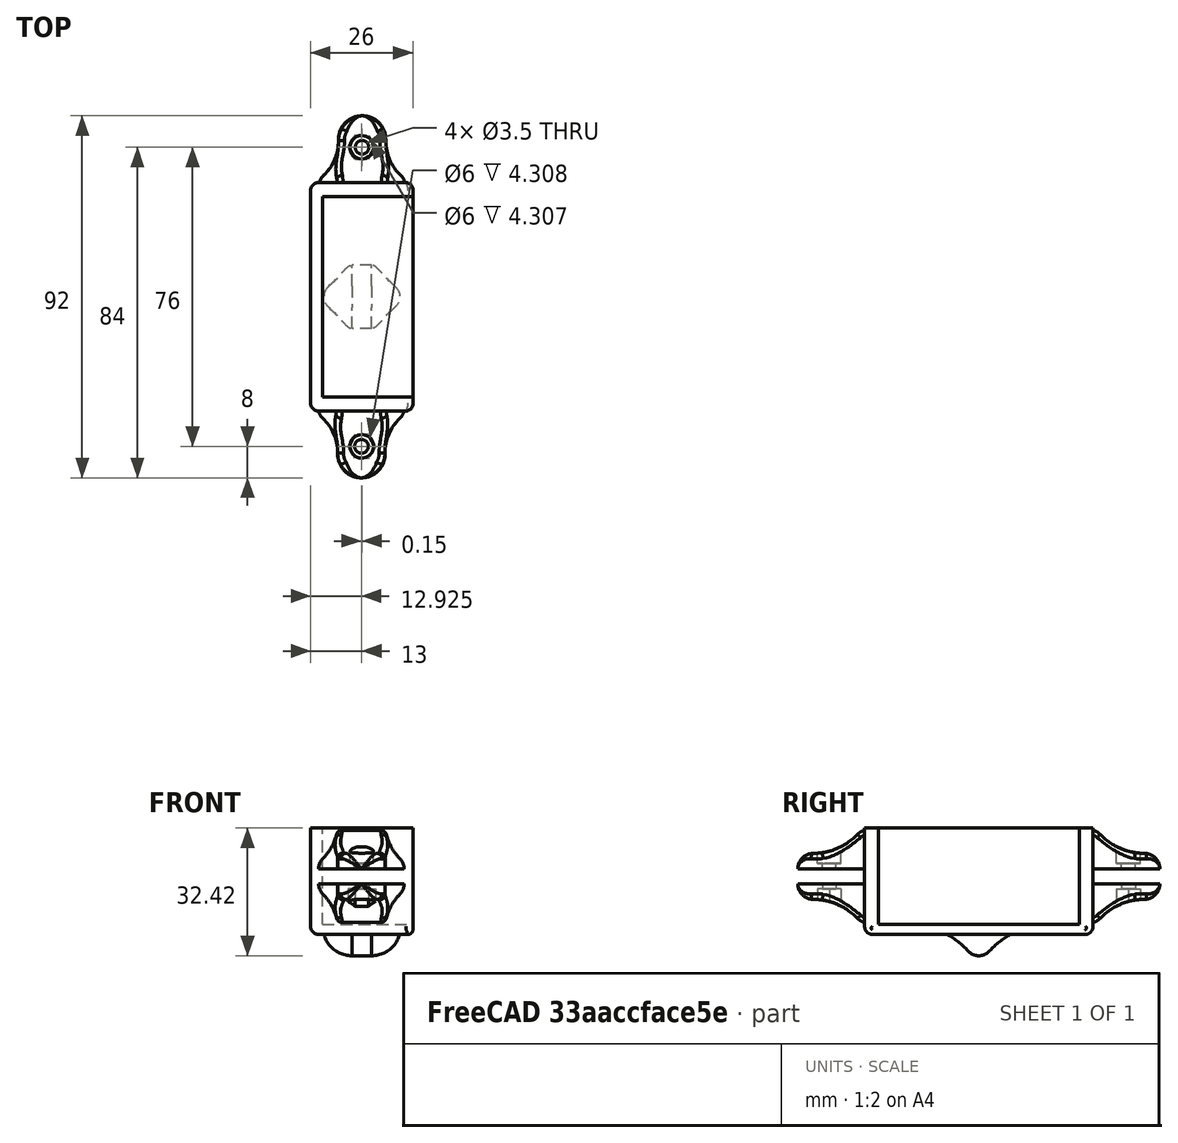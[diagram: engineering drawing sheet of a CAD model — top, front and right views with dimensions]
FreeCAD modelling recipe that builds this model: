
FCSTD DOCUMENT  (FreeCAD 0.16R6692 (Git))
Label: PortaBateriasCortado
License: All rights reserved
LicenseURL: http://es.wikipedia.org/wiki/Todos_los_derechos_reservados
objects: Sketcher::SketchObject×15, Part::MultiFuse×15, Part::Cut×12, PartDesign::Pad×9, Part::Cylinder×9, PartDesign::Revolution×6, Part::Fillet×6, Part::Box×5, Part::Sphere×2, Mesh::Feature×1, Part::Feature×1
note: 95 computed .brp shape members not serialized (recipe doc carries the construction recipe); baked Part::Feature solids carry a one-line shape summary decoded from their .brp

FEATURE [Mesh::Feature] EVOLUTION_Portapilas
FEATURE [Part::Box] Box017  label="Porta-Portapilas_Madre"
  Height = 60
  Length = 26
  Placement = pos=(-57,-29,-13) rot=(0,0,1;0rad)
  Width = 58
FEATURE [Part::Box] Box018  label="Hueco_portapilas"
  Height = 55
  Length = 26
  Placement = pos=(-54,-25.5,-10.5) rot=(0,0,1;0rad)
  Width = 51
FEATURE [Sketcher::SketchObject] Sketch014  label="Portapilas_rueda_loca"
  Placement = pos=(-46.5,0,0) rot=(0.57735,-0.57735,-0.57735;2.0944rad)
  sketch-geometry (6):
    g0: LineSegment [constr] StartX=0 StartY=0 StartZ=0 EndX=0 EndY=-13 EndZ=0
    g1: ArcOfCircle CenterX=0 CenterY=-16.7163 CenterZ=0 NormalX=0 NormalY=0 NormalZ=1 Radius=3.7 StartAngle=3.87448 EndAngle=5.55029
    g2: ArcOfCircle CenterX=17.6149 CenterY=-32.5721 CenterZ=0 NormalX=0 NormalY=0 NormalZ=1 Radius=20 StartAngle=1.77802 EndAngle=2.4087
    g3: ArcOfCircle CenterX=-17.6149 CenterY=-32.5721 CenterZ=0 NormalX=0 NormalY=0 NormalZ=1 Radius=20 StartAngle=0.73289 EndAngle=1.36357
    g4: LineSegment [constr] StartX=-2.75 StartY=-19.1917 StartZ=0 EndX=2.75 EndY=-19.1917 EndZ=0
    g5: LineSegment StartX=-13.5 StartY=-13 StartZ=0 EndX=13.5 EndY=-13 EndZ=0
  constraints (19):
    c: Coincident(g0,g-1)
    c: Vertical(g0)
    c: DistanceY(g0) = -13
    c: PointOnObject(g1,g-2)
    c: Coincident(g2,g1)
    c: Coincident(g4,g1)
    c: Horizontal(g4)
    c: Coincident(g1,g3)
    c: Symmetric(g3,g2,g0)
    c: Coincident(g4,g1)
    c: Tangent(g1,g3)
    c: Coincident(g5,g3)
    c: Coincident(g5,g2)
    c: DistanceX(g5) = 27
    c: PointOnObject(g0,g5)
    c: DistanceX(g4) = 5.5
    c: Radius(g3) = 20
    c: Equal(g2,g3)
    c: Radius(g1) = 3.7
FEATURE [PartDesign::Pad] Pad002  label="[Extrusion]_Rueda_Loca"
  Length = 5
  Length2 = 100
  Placement = pos=(-46.5,0,0) rot=(0.57735,-0.57735,-0.57735;2.0944rad)
  Reversed = true
  Sketch = -> Sketch014
  Type = 0
FEATURE [Sketcher::SketchObject] Sketch015  label="[Croquis]_Rueda_Loca_para_revolucion_1"
  Placement = pos=(-46.5,0,-13) rot=(0.57735,-0.57735,-0.57735;2.0944rad)
  sketch-geometry (5):
    g0: ArcOfCircle CenterX=0 CenterY=-3.71632 CenterZ=0 NormalX=0 NormalY=0 NormalZ=1 Radius=3.7 StartAngle=3.87448 EndAngle=5.55029
    g1: ArcOfCircle CenterX=17.6149 CenterY=-19.5721 CenterZ=0 NormalX=0 NormalY=0 NormalZ=1 Radius=20 StartAngle=1.77802 EndAngle=2.4087
    g2: ArcOfCircle CenterX=-17.6149 CenterY=-19.5721 CenterZ=0 NormalX=0 NormalY=0 NormalZ=1 Radius=20 StartAngle=0.732891 EndAngle=1.36357
    g3: LineSegment [constr] StartX=-2.75 StartY=-6.19169 StartZ=0 EndX=2.75 EndY=-6.19169 EndZ=0
    g4: LineSegment StartX=-13.5 StartY=0 StartZ=0 EndX=13.5 EndY=0 EndZ=0
  constraints (17):
    c: PointOnObject(g0,g-2)
    c: Coincident(g1,g0)
    c: Coincident(g3,g0)
    c: Horizontal(g3)
    c: Coincident(g0,g2)
    c: Coincident(g3,g0)
    c: Tangent(g0,g2)
    c: DistanceX(g3) = 5.5
    c: Radius(g2) = 20
    c: Equal(g1,g2)
    c: Radius(g0) = 3.7
    c: Coincident(g4,g2)
    c: Coincident(g4,g1)
    c: DistanceX(g4) = 27
    c: PointOnObject(g2,g-1)
    c: PointOnObject(g1,g-1)
    c: Symmetric(g2,g1,g-2)
FEATURE [PartDesign::Revolution] Revolution  label="[Revolucion]_Rueda_Loca_2"
  Angle = 90
  Axis = (0,-1,0)
  Base = (-46.5,0,-13)
  Placement = pos=(-46.5,0,-13) rot=(0.57735,-0.57735,-0.57735;2.0944rad)
  ReferenceAxis = -> Sketch015 [H_Axis]
  Reversed = true
  Sketch = -> Sketch015
FEATURE [Sketcher::SketchObject] Sketch016  label="[Croquis]_Rueda_Loca_para_revolucion_2"
  Placement = pos=(-41.5,0,-13) rot=(0.57735,-0.57735,-0.57735;2.0944rad)
  sketch-geometry (5):
    g0: ArcOfCircle CenterX=0 CenterY=-3.71632 CenterZ=0 NormalX=0 NormalY=0 NormalZ=1 Radius=3.7 StartAngle=3.87448 EndAngle=5.55029
    g1: ArcOfCircle CenterX=17.6149 CenterY=-19.5721 CenterZ=0 NormalX=0 NormalY=0 NormalZ=1 Radius=20 StartAngle=1.77802 EndAngle=2.4087
    g2: ArcOfCircle CenterX=-17.6149 CenterY=-19.5721 CenterZ=0 NormalX=0 NormalY=0 NormalZ=1 Radius=20 StartAngle=0.732891 EndAngle=1.36357
    g3: LineSegment [constr] StartX=-2.75 StartY=-6.19169 StartZ=0 EndX=2.75 EndY=-6.19169 EndZ=0
    g4: LineSegment StartX=-13.5 StartY=0 StartZ=0 EndX=13.5 EndY=-1e-12 EndZ=0
  constraints (17):
    c: PointOnObject(g0,g-2)
    c: Coincident(g1,g0)
    c: Coincident(g3,g0)
    c: Horizontal(g3)
    c: Coincident(g0,g2)
    c: Coincident(g3,g0)
    c: Tangent(g0,g2)
    c: DistanceX(g3) = 5.5
    c: Radius(g2) = 20
    c: Equal(g1,g2)
    c: Radius(g0) = 3.7
    c: Coincident(g4,g2)
    c: Coincident(g4,g1)
    c: DistanceX(g4) = 27
    c: PointOnObject(g2,g-1)
    c: PointOnObject(g1,g-1)
    c: Symmetric(g2,g1,g-2)
FEATURE [PartDesign::Revolution] Revolution001  label="[Revolucion]_Rueda_Loca_1"
  Angle = 90
  Axis = (0,-1,0)
  Base = (-41.5,0,-13)
  Placement = pos=(-41.5,0,-13) rot=(0.57735,-0.57735,-0.57735;2.0944rad)
  ReferenceAxis = -> Sketch016 [H_Axis]
  Sketch = -> Sketch016
FEATURE [Part::Sphere] Sphere  label="Porta-Portapilas_Hueco_Dedo_1"
  Angle1 = -90
  Angle2 = 90
  Angle3 = 360
  Placement = pos=(-47,35,22) rot=(0,0,1;0rad)
  Radius = 9
FEATURE [Part::Sphere] Sphere001  label="Porta-Portapilas_Hueco_Dedo_2"
  Angle1 = -90
  Angle2 = 90
  Angle3 = 360
  Placement = pos=(-47,-35,22) rot=(0,0,1;0rad)
  Radius = 9
FEATURE [Part::MultiFuse] Fusion017  label="[Union]_Porta-Portapilas_Dedo"
  Placement = pos=(0,0,2) rot=(0,0,1;0rad)
  Shapes = -> [Sphere,Sphere001]
FEATURE [Part::Cylinder] Cylinder020  label="Porta-Portapilas_Cilindro_Cables"
  Angle = 360
  Height = 4
  Placement = pos=(-43,-11.5,43) rot=(0,0,1;0rad)
  Radius = 5
FEATURE [Part::Box] Box019  label="Porta-Portapilas_Cubo_Cables"
  Height = 4
  Length = 20
  Placement = pos=(-43,-16.5,43) rot=(0,0,1;0rad)
  Width = 10
FEATURE [Sketcher::SketchObject] Sketch036
  sketch-geometry (8):
    g0: ArcOfCircle CenterX=-85.1605 CenterY=0 CenterZ=0 NormalX=0 NormalY=0 NormalZ=1 Radius=4 StartAngle=3.14159 EndAngle=3.95469
    g1: ArcOfCircle CenterX=-96.1565 CenterY=-11.6227 CenterZ=0 NormalX=0 NormalY=0 NormalZ=1 Radius=12 StartAngle=6.26222 EndAngle=7.09628
    g2: ArcOfCircle CenterX=-78.1605 CenterY=-12 CenterZ=0 NormalX=0 NormalY=0 NormalZ=1 Radius=6 StartAngle=3.12063 EndAngle=6.30415
    g3: ArcOfCircle CenterX=-71.1605 CenterY=-7.788e-09 CenterZ=0 NormalX=0 NormalY=0 NormalZ=1 Radius=4 StartAngle=5.47009 EndAngle=6.28319
    g4: ArcOfCircle CenterX=-60.1645 CenterY=-11.6227 CenterZ=0 NormalX=0 NormalY=0 NormalZ=1 Radius=12 StartAngle=2.3285 EndAngle=3.16255
    g5: LineSegment [constr] StartX=-78.1605 StartY=0 StartZ=0 EndX=-78.1605 EndY=-18 EndZ=0
    g6: LineSegment StartX=-89.1605 StartY=0 StartZ=0 EndX=-78.1605 EndY=0 EndZ=0
    g7: LineSegment StartX=-78.1605 StartY=0 StartZ=0 EndX=-67.1605 EndY=0 EndZ=0
  constraints (27):
    c: Coincident(g1,g0)
    c: Coincident(g2,g1)
    c: Coincident(g4,g3)
    c: Coincident(g4,g2)
    c: Tangent(g1,g2)
    c: Tangent(g4,g2)
    c: Tangent(g4,g3)
    c: Tangent(g1,g0)
    c: Equal(g0,g3)
    c: Vertical(g5)
    c: Symmetric(g1,g2,g5)
    c: Symmetric(g0,g3,g5)
    c: PointOnObject(g5,g2)
    c: Coincident(g6,g0)
    c: Coincident(g6,g5)
    c: Horizontal(g6)
    c: Coincident(g7,g5)
    c: Coincident(g7,g3)
    c: Horizontal(g7)
    c: DistanceX(g7) = 11
    c: Radius(g2) = 6
    c: Perpendicular(g0,g6)
    c: DistanceY(g5) = -18
    c: Radius(g1) = 12
    c: Radius(g0) = 4
    c: PointOnObject(g5,g-1)
    c: DistanceX(g-1,g3) = -67.1605
FEATURE [Sketcher::SketchObject] Sketch037
  Placement = pos=(-66,0,0) rot=(0.57735,-0.57735,-0.57735;2.0944rad)
  sketch-geometry (6):
    g0: ArcOfCircle CenterX=14.0605 CenterY=19.4746 CenterZ=0 NormalX=0 NormalY=0 NormalZ=1 Radius=15.4747 StartAngle=3.90571 EndAngle=4.70928
    g1: ArcOfCircle CenterX=0 CenterY=6 CenterZ=0 NormalX=0 NormalY=0 NormalZ=1 Radius=4 StartAngle=0.764125 EndAngle=1.5708
    g2: LineSegment StartX=0 StartY=18 StartZ=0 EndX=18 EndY=18 EndZ=0
    g3: LineSegment StartX=18 StartY=0 StartZ=0 EndX=18 EndY=18 EndZ=0
    g4: ArcOfCircle CenterX=14 CenterY=0 CenterZ=0 NormalX=0 NormalY=0 NormalZ=1 Radius=4 StartAngle=0 EndAngle=1.56769
    g5: LineSegment StartX=0 StartY=10 StartZ=0 EndX=0 EndY=18 EndZ=0
  constraints (21):
    c: Coincident(g1,g0)
    c: Tangent(g0,g1)
    c: PointOnObject(g3,g-1)
    c: PointOnObject(g1,g-2)
    c: Perpendicular(g1,g-2)
    c: Horizontal(g2)
    c: Vertical(g3)
    c: Coincident(g2,g3)
    c: PointOnObject(g4,g-1)
    c: Coincident(g4,g0)
    c: Coincident(g4,g3)
    c: Equal(g4,g1)
    c: Radius(g4) = 4
    c: Tangent(g4,g0)
    c: DistanceY(g3) = 18
    c: PointOnObject(g5,g-2)
    c: Vertical(g5)
    c: Coincident(g1,g5)
    c: Coincident(g2,g5)
    c: DistanceX(g2) = 18
    c: DistanceY(g5) = 8
FEATURE [Part::Cylinder] Cylinder045  label="Cylinder"
  Angle = 360
  Height = 10
  Placement = pos=(-44,-38,-2) rot=(0,0,1;0rad)
  Radius = 1.75
FEATURE [Part::Cylinder] Cylinder048  label="Cylinder004"
  Angle = 360
  Height = 8
  Placement = pos=(-44,-38,5) rot=(0,0,1;0rad)
  Radius = 2.75
FEATURE [Part::Feature] bq_logo007_solid  label="bq_logo002 (Solid)"
  Placement = pos=(-56,0,15) rot=(-0.57735,-0.57735,0.57735;2.0944rad)
  shape: bbox 3 x 25 x 21.48 mm, 152 faces (baked)
FEATURE [Part::MultiFuse] Fusion025  label="[Fusion]Porta-Portapilas_Cables"
  Placement = pos=(0,0,0.5) rot=(0,0,1;0rad)
  Shapes = -> [Box019,Cylinder020]
FEATURE [PartDesign::Revolution] Revolution002
  Angle = 90
  Axis = (1,0,0)
  Base = (0,0,0)
  ReferenceAxis = -> Sketch036 [H_Axis]
  Reversed = true
  Sketch = -> Sketch036
FEATURE [PartDesign::Pad] Pad017
  Length = 25
  Length2 = 100
  Placement = pos=(-66,0,0) rot=(0.57735,-0.57735,-0.57735;2.0944rad)
  Sketch = -> Sketch037
  Type = 0
FEATURE [Part::Cut] Cut048002
  Base = -> Revolution002
  Placement = pos=(34.1,-28,3.6) rot=(0,0,1;0rad)
  Tool = -> Pad017
FEATURE [Part::MultiFuse] Fusion055002
  Placement = pos=(-0.025,0,0) rot=(0,0,1;0rad)
  Shapes = -> [Cylinder048,Cylinder045]
FEATURE [Part::Fillet] Fillet036
  Base = -> Cut048002
  Edges = 2 edges r=1.5: [Edge8,Edge21]
FEATURE [Sketcher::SketchObject] Sketch049
  sketch-geometry (8):
    g0: ArcOfCircle CenterX=-85.1605 CenterY=0 CenterZ=0 NormalX=0 NormalY=0 NormalZ=1 Radius=4 StartAngle=3.14159 EndAngle=3.95469
    g1: ArcOfCircle CenterX=-96.1565 CenterY=-11.6227 CenterZ=0 NormalX=0 NormalY=0 NormalZ=1 Radius=12 StartAngle=6.26222 EndAngle=7.09628
    g2: ArcOfCircle CenterX=-78.1605 CenterY=-12 CenterZ=0 NormalX=0 NormalY=0 NormalZ=1 Radius=6 StartAngle=3.12063 EndAngle=6.30415
    g3: ArcOfCircle CenterX=-71.1605 CenterY=-7.788e-09 CenterZ=0 NormalX=0 NormalY=0 NormalZ=1 Radius=4 StartAngle=5.47009 EndAngle=6.28319
    g4: ArcOfCircle CenterX=-60.1645 CenterY=-11.6227 CenterZ=0 NormalX=0 NormalY=0 NormalZ=1 Radius=12 StartAngle=2.3285 EndAngle=3.16255
    g5: LineSegment [constr] StartX=-78.1605 StartY=0 StartZ=0 EndX=-78.1605 EndY=-18 EndZ=0
    g6: LineSegment StartX=-89.1605 StartY=0 StartZ=0 EndX=-78.1605 EndY=0 EndZ=0
    g7: LineSegment StartX=-78.1605 StartY=0 StartZ=0 EndX=-67.1605 EndY=0 EndZ=0
  constraints (27):
    c: Coincident(g1,g0)
    c: Coincident(g2,g1)
    c: Coincident(g4,g3)
    c: Coincident(g4,g2)
    c: Tangent(g1,g2)
    c: Tangent(g4,g2)
    c: Tangent(g4,g3)
    c: Tangent(g1,g0)
    c: Equal(g0,g3)
    c: Vertical(g5)
    c: Symmetric(g1,g2,g5)
    c: Symmetric(g0,g3,g5)
    c: PointOnObject(g5,g2)
    c: Coincident(g6,g0)
    c: Coincident(g6,g5)
    c: Horizontal(g6)
    c: Coincident(g7,g5)
    c: Coincident(g7,g3)
    c: Horizontal(g7)
    c: DistanceX(g7) = 11
    c: Radius(g2) = 6
    c: Perpendicular(g0,g6)
    c: DistanceY(g5) = -18
    c: Radius(g1) = 12
    c: Radius(g0) = 4
    c: PointOnObject(g5,g-1)
    c: DistanceX(g-1,g3) = -67.1605
FEATURE [Sketcher::SketchObject] Sketch050
  Placement = pos=(-66,0,0) rot=(0.57735,-0.57735,-0.57735;2.0944rad)
  sketch-geometry (6):
    g0: ArcOfCircle CenterX=14.0605 CenterY=19.4746 CenterZ=0 NormalX=0 NormalY=0 NormalZ=1 Radius=15.4747 StartAngle=3.90571 EndAngle=4.70928
    g1: ArcOfCircle CenterX=0 CenterY=6 CenterZ=0 NormalX=0 NormalY=0 NormalZ=1 Radius=4 StartAngle=0.764125 EndAngle=1.5708
    g2: LineSegment StartX=0 StartY=18 StartZ=0 EndX=18 EndY=18 EndZ=0
    g3: LineSegment StartX=18 StartY=0 StartZ=0 EndX=18 EndY=18 EndZ=0
    g4: ArcOfCircle CenterX=14 CenterY=0 CenterZ=0 NormalX=0 NormalY=0 NormalZ=1 Radius=4 StartAngle=0 EndAngle=1.56769
    g5: LineSegment StartX=0 StartY=10 StartZ=0 EndX=0 EndY=18 EndZ=0
  constraints (21):
    c: Coincident(g1,g0)
    c: Tangent(g0,g1)
    c: PointOnObject(g3,g-1)
    c: PointOnObject(g1,g-2)
    c: Perpendicular(g1,g-2)
    c: Horizontal(g2)
    c: Vertical(g3)
    c: Coincident(g2,g3)
    c: PointOnObject(g4,g-1)
    c: Coincident(g4,g0)
    c: Coincident(g4,g3)
    c: Equal(g4,g1)
    c: Radius(g4) = 4
    c: Tangent(g4,g0)
    c: DistanceY(g3) = 18
    c: PointOnObject(g5,g-2)
    c: Vertical(g5)
    c: Coincident(g1,g5)
    c: Coincident(g2,g5)
    c: DistanceX(g2) = 18
    c: DistanceY(g5) = 8
FEATURE [PartDesign::Revolution] Revolution003
  Angle = 90
  Axis = (1,0,0)
  Base = (0,0,0)
  ReferenceAxis = -> Sketch049 [H_Axis]
  Reversed = true
  Sketch = -> Sketch049
FEATURE [PartDesign::Pad] Pad018
  Length = 25
  Length2 = 100
  Placement = pos=(-66,0,0) rot=(0.57735,-0.57735,-0.57735;2.0944rad)
  Sketch = -> Sketch050
  Type = 0
FEATURE [Part::Cut] Cut048003
  Base = -> Revolution003
  Placement = pos=(34.1,-28,3.6) rot=(0,0,1;0rad)
  Tool = -> Pad018
FEATURE [Part::Fillet] Fillet037
  Base = -> Cut048003
  Edges = 2 edges r=1.5: [Edge8,Edge21]
FEATURE [Part::Cut] Cut048004  label="Rail_superior"
  Base = -> Fillet036
  Placement = pos=(-0.05,0,0) rot=(0,0,1;0rad)
  Tool = -> Fusion055002
FEATURE [Part::Cylinder] Cylinder054  label="Cylinder058"
  Angle = 360
  Height = 10
  Placement = pos=(-44,-38,-2) rot=(0,0,1;0rad)
  Radius = 1.75
FEATURE [Sketcher::SketchObject] Sketch051
  Placement = pos=(-44,-38,13) rot=(0,0,1;0rad)
  sketch-geometry (7):
    g0: LineSegment StartX=-1.65 StartY=2.85788 StartZ=0 EndX=-3.3 EndY=0 EndZ=0
    g1: LineSegment StartX=-3.3 StartY=0 StartZ=0 EndX=-1.65 EndY=-2.85788 EndZ=0
    g2: LineSegment StartX=-1.65 StartY=-2.85788 StartZ=0 EndX=1.65 EndY=-2.85788 EndZ=0
    g3: LineSegment StartX=1.65 StartY=-2.85788 StartZ=0 EndX=3.3 EndY=0 EndZ=0
    g4: LineSegment StartX=3.3 StartY=0 StartZ=0 EndX=1.65 EndY=2.85788 EndZ=0
    g5: LineSegment StartX=1.65 StartY=2.85788 StartZ=0 EndX=-1.65 EndY=2.85788 EndZ=0
    g6: Circle [constr] CenterX=0 CenterY=0 CenterZ=0 NormalX=0 NormalY=0 NormalZ=1 Radius=3.3
  constraints (17):
    c: Coincident(g0,g1)
    c: Coincident(g1,g2)
    c: Coincident(g2,g3)
    c: Coincident(g3,g4)
    c: Coincident(g4,g5)
    c: Coincident(g5,g0)
    c: Equal(g0, g1-g5) x5
    c: PointOnObject(g0,g6)
    c: PointOnObject(g1,g6)
    c: PointOnObject(g2,g6)
    c: PointOnObject(g3,g6)
    c: PointOnObject(g4,g6)
    c: PointOnObject(g5,g6)
    c: Coincident(g3,g-1)
    c: Radius(g6) = 3.3
    c: Horizontal(g5)
    c: Coincident(g6,g-1)
FEATURE [PartDesign::Pad] Pad019
  Length = 8
  Length2 = 100
  Placement = pos=(-44,-38,13) rot=(0,0,1;0rad)
  Reversed = true
  Sketch = -> Sketch051
  Type = 0
FEATURE [Part::MultiFuse] Fusion055003
  Placement = pos=(-0.075,0,0) rot=(0,0,1;0rad)
  Shapes = -> [Pad019,Cylinder054]
FEATURE [Part::Cut] Cut048005  label="Rail_inferior"
  Base = -> Fillet037
  Placement = pos=(-88.15,0,3.5) rot=(0,1,0;3.14159rad)
  Tool = -> Fusion055003
FEATURE [Part::MultiFuse] Fusion055004  label="Rail_izquierdo"
  Shapes = -> [Cut048004,Cut048005]
FEATURE [Sketcher::SketchObject] Sketch052
  sketch-geometry (8):
    g0: ArcOfCircle CenterX=-85.1605 CenterY=0 CenterZ=0 NormalX=0 NormalY=0 NormalZ=1 Radius=4 StartAngle=3.14159 EndAngle=3.95469
    g1: ArcOfCircle CenterX=-96.1565 CenterY=-11.6227 CenterZ=0 NormalX=0 NormalY=0 NormalZ=1 Radius=12 StartAngle=6.26222 EndAngle=7.09628
    g2: ArcOfCircle CenterX=-78.1605 CenterY=-12 CenterZ=0 NormalX=0 NormalY=0 NormalZ=1 Radius=6 StartAngle=3.12063 EndAngle=6.30415
    g3: ArcOfCircle CenterX=-71.1605 CenterY=-7.788e-09 CenterZ=0 NormalX=0 NormalY=0 NormalZ=1 Radius=4 StartAngle=5.47009 EndAngle=6.28319
    g4: ArcOfCircle CenterX=-60.1645 CenterY=-11.6227 CenterZ=0 NormalX=0 NormalY=0 NormalZ=1 Radius=12 StartAngle=2.3285 EndAngle=3.16255
    g5: LineSegment [constr] StartX=-78.1605 StartY=0 StartZ=0 EndX=-78.1605 EndY=-18 EndZ=0
    g6: LineSegment StartX=-89.1605 StartY=0 StartZ=0 EndX=-78.1605 EndY=0 EndZ=0
    g7: LineSegment StartX=-78.1605 StartY=0 StartZ=0 EndX=-67.1605 EndY=0 EndZ=0
  constraints (27):
    c: Coincident(g1,g0)
    c: Coincident(g2,g1)
    c: Coincident(g4,g3)
    c: Coincident(g4,g2)
    c: Tangent(g1,g2)
    c: Tangent(g4,g2)
    c: Tangent(g4,g3)
    c: Tangent(g1,g0)
    c: Equal(g0,g3)
    c: Vertical(g5)
    c: Symmetric(g1,g2,g5)
    c: Symmetric(g0,g3,g5)
    c: PointOnObject(g5,g2)
    c: Coincident(g6,g0)
    c: Coincident(g6,g5)
    c: Horizontal(g6)
    c: Coincident(g7,g5)
    c: Coincident(g7,g3)
    c: Horizontal(g7)
    c: DistanceX(g7) = 11
    c: Radius(g2) = 6
    c: Perpendicular(g0,g6)
    c: DistanceY(g5) = -18
    c: Radius(g1) = 12
    c: Radius(g0) = 4
    c: PointOnObject(g5,g-1)
    c: DistanceX(g-1,g3) = -67.1605
FEATURE [Sketcher::SketchObject] Sketch053
  Placement = pos=(-66,0,0) rot=(0.57735,-0.57735,-0.57735;2.0944rad)
  sketch-geometry (6):
    g0: ArcOfCircle CenterX=14.0605 CenterY=19.4746 CenterZ=0 NormalX=0 NormalY=0 NormalZ=1 Radius=15.4747 StartAngle=3.90571 EndAngle=4.70928
    g1: ArcOfCircle CenterX=0 CenterY=6 CenterZ=0 NormalX=0 NormalY=0 NormalZ=1 Radius=4 StartAngle=0.764125 EndAngle=1.5708
    g2: LineSegment StartX=0 StartY=18 StartZ=0 EndX=18 EndY=18 EndZ=0
    g3: LineSegment StartX=18 StartY=0 StartZ=0 EndX=18 EndY=18 EndZ=0
    g4: ArcOfCircle CenterX=14 CenterY=0 CenterZ=0 NormalX=0 NormalY=0 NormalZ=1 Radius=4 StartAngle=0 EndAngle=1.56769
    g5: LineSegment StartX=0 StartY=10 StartZ=0 EndX=0 EndY=18 EndZ=0
  constraints (21):
    c: Coincident(g1,g0)
    c: Tangent(g0,g1)
    c: PointOnObject(g3,g-1)
    c: PointOnObject(g1,g-2)
    c: Perpendicular(g1,g-2)
    c: Horizontal(g2)
    c: Vertical(g3)
    c: Coincident(g2,g3)
    c: PointOnObject(g4,g-1)
    c: Coincident(g4,g0)
    c: Coincident(g4,g3)
    c: Equal(g4,g1)
    c: Radius(g4) = 4
    c: Tangent(g4,g0)
    c: DistanceY(g3) = 18
    c: PointOnObject(g5,g-2)
    c: Vertical(g5)
    c: Coincident(g1,g5)
    c: Coincident(g2,g5)
    c: DistanceX(g2) = 18
    c: DistanceY(g5) = 8
FEATURE [Part::Cylinder] Cylinder055  label="Cylinder062"
  Angle = 360
  Height = 10
  Placement = pos=(-44,-38,-2) rot=(0,0,1;0rad)
  Radius = 1.75
FEATURE [Part::Cylinder] Cylinder056  label="Cylinder060"
  Angle = 360
  Height = 8
  Placement = pos=(-44,-38,5) rot=(0,0,1;0rad)
  Radius = 2.75
FEATURE [PartDesign::Revolution] Revolution004
  Angle = 90
  Axis = (1,0,0)
  Base = (0,0,0)
  ReferenceAxis = -> Sketch052 [H_Axis]
  Reversed = true
  Sketch = -> Sketch052
FEATURE [PartDesign::Pad] Pad020
  Length = 25
  Length2 = 100
  Placement = pos=(-66,0,0) rot=(0.57735,-0.57735,-0.57735;2.0944rad)
  Sketch = -> Sketch053
  Type = 0
FEATURE [Part::Cut] Cut048006
  Base = -> Revolution004
  Placement = pos=(34.1,-28,3.6) rot=(0,0,1;0rad)
  Tool = -> Pad020
FEATURE [Part::MultiFuse] Fusion055005
  Placement = pos=(-0.025,0,0) rot=(0,0,1;0rad)
  Shapes = -> [Cylinder056,Cylinder055]
FEATURE [Part::Fillet] Fillet038
  Base = -> Cut048006
  Edges = 2 edges r=1.5: [Edge8,Edge21]
FEATURE [Sketcher::SketchObject] Sketch054
  sketch-geometry (8):
    g0: ArcOfCircle CenterX=-85.1605 CenterY=0 CenterZ=0 NormalX=0 NormalY=0 NormalZ=1 Radius=4 StartAngle=3.14159 EndAngle=3.95469
    g1: ArcOfCircle CenterX=-96.1565 CenterY=-11.6227 CenterZ=0 NormalX=0 NormalY=0 NormalZ=1 Radius=12 StartAngle=6.26222 EndAngle=7.09628
    g2: ArcOfCircle CenterX=-78.1605 CenterY=-12 CenterZ=0 NormalX=0 NormalY=0 NormalZ=1 Radius=6 StartAngle=3.12063 EndAngle=6.30415
    g3: ArcOfCircle CenterX=-71.1605 CenterY=-7.788e-09 CenterZ=0 NormalX=0 NormalY=0 NormalZ=1 Radius=4 StartAngle=5.47009 EndAngle=6.28319
    g4: ArcOfCircle CenterX=-60.1645 CenterY=-11.6227 CenterZ=0 NormalX=0 NormalY=0 NormalZ=1 Radius=12 StartAngle=2.3285 EndAngle=3.16255
    g5: LineSegment [constr] StartX=-78.1605 StartY=0 StartZ=0 EndX=-78.1605 EndY=-18 EndZ=0
    g6: LineSegment StartX=-89.1605 StartY=0 StartZ=0 EndX=-78.1605 EndY=0 EndZ=0
    g7: LineSegment StartX=-78.1605 StartY=0 StartZ=0 EndX=-67.1605 EndY=0 EndZ=0
  constraints (27):
    c: Coincident(g1,g0)
    c: Coincident(g2,g1)
    c: Coincident(g4,g3)
    c: Coincident(g4,g2)
    c: Tangent(g1,g2)
    c: Tangent(g4,g2)
    c: Tangent(g4,g3)
    c: Tangent(g1,g0)
    c: Equal(g0,g3)
    c: Vertical(g5)
    c: Symmetric(g1,g2,g5)
    c: Symmetric(g0,g3,g5)
    c: PointOnObject(g5,g2)
    c: Coincident(g6,g0)
    c: Coincident(g6,g5)
    c: Horizontal(g6)
    c: Coincident(g7,g5)
    c: Coincident(g7,g3)
    c: Horizontal(g7)
    c: DistanceX(g7) = 11
    c: Radius(g2) = 6
    c: Perpendicular(g0,g6)
    c: DistanceY(g5) = -18
    c: Radius(g1) = 12
    c: Radius(g0) = 4
    c: PointOnObject(g5,g-1)
    c: DistanceX(g-1,g3) = -67.1605
FEATURE [Sketcher::SketchObject] Sketch055
  Placement = pos=(-66,0,0) rot=(0.57735,-0.57735,-0.57735;2.0944rad)
  sketch-geometry (6):
    g0: ArcOfCircle CenterX=14.0605 CenterY=19.4746 CenterZ=0 NormalX=0 NormalY=0 NormalZ=1 Radius=15.4747 StartAngle=3.90571 EndAngle=4.70928
    g1: ArcOfCircle CenterX=0 CenterY=6 CenterZ=0 NormalX=0 NormalY=0 NormalZ=1 Radius=4 StartAngle=0.764125 EndAngle=1.5708
    g2: LineSegment StartX=0 StartY=18 StartZ=0 EndX=18 EndY=18 EndZ=0
    g3: LineSegment StartX=18 StartY=0 StartZ=0 EndX=18 EndY=18 EndZ=0
    g4: ArcOfCircle CenterX=14 CenterY=0 CenterZ=0 NormalX=0 NormalY=0 NormalZ=1 Radius=4 StartAngle=0 EndAngle=1.56769
    g5: LineSegment StartX=0 StartY=10 StartZ=0 EndX=0 EndY=18 EndZ=0
  constraints (21):
    c: Coincident(g1,g0)
    c: Tangent(g0,g1)
    c: PointOnObject(g3,g-1)
    c: PointOnObject(g1,g-2)
    c: Perpendicular(g1,g-2)
    c: Horizontal(g2)
    c: Vertical(g3)
    c: Coincident(g2,g3)
    c: PointOnObject(g4,g-1)
    c: Coincident(g4,g0)
    c: Coincident(g4,g3)
    c: Equal(g4,g1)
    c: Radius(g4) = 4
    c: Tangent(g4,g0)
    c: DistanceY(g3) = 18
    c: PointOnObject(g5,g-2)
    c: Vertical(g5)
    c: Coincident(g1,g5)
    c: Coincident(g2,g5)
    c: DistanceX(g2) = 18
    c: DistanceY(g5) = 8
FEATURE [PartDesign::Revolution] Revolution005
  Angle = 90
  Axis = (1,0,0)
  Base = (0,0,0)
  ReferenceAxis = -> Sketch054 [H_Axis]
  Reversed = true
  Sketch = -> Sketch054
FEATURE [PartDesign::Pad] Pad021
  Length = 25
  Length2 = 100
  Placement = pos=(-66,0,0) rot=(0.57735,-0.57735,-0.57735;2.0944rad)
  Sketch = -> Sketch055
  Type = 0
FEATURE [Part::Cut] Cut048007
  Base = -> Revolution005
  Placement = pos=(34.1,-28,3.6) rot=(0,0,1;0rad)
  Tool = -> Pad021
FEATURE [Part::Fillet] Fillet039
  Base = -> Cut048007
  Edges = 2 edges r=1.5: [Edge8,Edge21]
FEATURE [Part::Cut] Cut048008  label="Rail_superior001"
  Base = -> Fillet038
  Placement = pos=(-0.05,0,0) rot=(0,0,1;0rad)
  Tool = -> Fusion055005
FEATURE [Part::Cylinder] Cylinder057  label="Cylinder063"
  Angle = 360
  Height = 10
  Placement = pos=(-44,-38,-2) rot=(0,0,1;0rad)
  Radius = 1.75
FEATURE [Sketcher::SketchObject] Sketch056
  Placement = pos=(-44,-38,13) rot=(0,0,1;0rad)
  sketch-geometry (7):
    g0: LineSegment StartX=-1.65 StartY=2.85788 StartZ=0 EndX=-3.3 EndY=0 EndZ=0
    g1: LineSegment StartX=-3.3 StartY=0 StartZ=0 EndX=-1.65 EndY=-2.85788 EndZ=0
    g2: LineSegment StartX=-1.65 StartY=-2.85788 StartZ=0 EndX=1.65 EndY=-2.85788 EndZ=0
    g3: LineSegment StartX=1.65 StartY=-2.85788 StartZ=0 EndX=3.3 EndY=0 EndZ=0
    g4: LineSegment StartX=3.3 StartY=0 StartZ=0 EndX=1.65 EndY=2.85788 EndZ=0
    g5: LineSegment StartX=1.65 StartY=2.85788 StartZ=0 EndX=-1.65 EndY=2.85788 EndZ=0
    g6: Circle [constr] CenterX=0 CenterY=0 CenterZ=0 NormalX=0 NormalY=0 NormalZ=1 Radius=3.3
  constraints (17):
    c: Coincident(g0,g1)
    c: Coincident(g1,g2)
    c: Coincident(g2,g3)
    c: Coincident(g3,g4)
    c: Coincident(g4,g5)
    c: Coincident(g5,g0)
    c: Equal(g0, g1-g5) x5
    c: PointOnObject(g0,g6)
    c: PointOnObject(g1,g6)
    c: PointOnObject(g2,g6)
    c: PointOnObject(g3,g6)
    c: PointOnObject(g4,g6)
    c: PointOnObject(g5,g6)
    c: Coincident(g3,g-1)
    c: Radius(g6) = 3.3
    c: Horizontal(g5)
    c: Coincident(g6,g-1)
FEATURE [PartDesign::Pad] Pad022
  Length = 8
  Length2 = 100
  Placement = pos=(-44,-38,13) rot=(0,0,1;0rad)
  Reversed = true
  Sketch = -> Sketch056
  Type = 0
FEATURE [Part::MultiFuse] Fusion055006
  Placement = pos=(-0.075,0,0) rot=(0,0,1;0rad)
  Shapes = -> [Pad022,Cylinder057]
FEATURE [Part::Cut] Cut048009  label="Rail_inferior001"
  Base = -> Fillet039
  Placement = pos=(-88.15,0,3.5) rot=(0,1,0;3.14159rad)
  Tool = -> Fusion055006
FEATURE [Part::MultiFuse] Fusion055007  label="Rail_iderecho"
  Placement = pos=(-88,0,0) rot=(0,0,1;3.14159rad)
  Shapes = -> [Cut048008,Cut048009]
FEATURE [Part::MultiFuse] Fusion055008  label="Rueda_loca"
  Placement = pos=(0,0,2) rot=(0,0,1;0rad)
  Shapes = -> [Pad002,Revolution001,Revolution]
FEATURE [Part::MultiFuse] Fusion055009  label="Huecos_portapilas"
  Shapes = -> [Box018,bq_logo007_solid,Fusion025]
FEATURE [Part::Cut] Cut048010
  Base = -> Box017
  Tool = -> Fusion055009
FEATURE [Part::Fillet] Fillet040
  Base = -> Cut048010
  Edges = 17 edges: [Edge1 r=2,Edge2 r=2,Edge3 r=2,Edge4 r=2,Edge103 r=2,Edge104 r=1.8,Edge105 r=2,Edge106 r=2,Edge107 r=1.2,Edge108 r=1.2,Edge109 r=1.2,Edge110 r=1.2,Edge111 r=1.2,Edge112 r=2,Edge113 r=1.2,Edge114 r=1.8,Edge322 r=1.2]
FEATURE [Part::Cut] Cut048011
  Base = -> Fillet040
  Tool = -> Fusion017
FEATURE [Part::Fillet] Fillet041
  Base = -> Cut048011
  Edges = 2 edges r=2: [Edge318,Edge336]
FEATURE [Part::MultiFuse] Fusion055010  label="PORTA-PORTAPILAS_FINAL"
  Shapes = -> [Fusion055004,Fillet041,Fusion055008,Fusion055007]
FEATURE [Part::Cylinder] Cylinder059  label="Cylinder064"
  Angle = 360
  Height = 8
  Placement = pos=(-44,38,5) rot=(0,0,1;0rad)
  Radius = 3
FEATURE [Sketcher::SketchObject] Sketch058
  Placement = pos=(0,0,-1.45) rot=(1,0,0;3.14159rad)
  sketch-geometry (7):
    g0: LineSegment StartX=-47.5 StartY=-38 StartZ=0 EndX=-45.75 EndY=-41.0311 EndZ=0
    g1: LineSegment StartX=-45.75 StartY=-41.0311 StartZ=0 EndX=-42.25 EndY=-41.0311 EndZ=0
    g2: LineSegment StartX=-42.25 StartY=-41.0311 StartZ=0 EndX=-40.5 EndY=-38 EndZ=0
    g3: LineSegment StartX=-40.5 StartY=-38 StartZ=0 EndX=-42.25 EndY=-34.9689 EndZ=0
    g4: LineSegment StartX=-42.25 StartY=-34.9689 StartZ=0 EndX=-45.75 EndY=-34.9689 EndZ=0
    g5: LineSegment StartX=-45.75 StartY=-34.9689 StartZ=0 EndX=-47.5 EndY=-38 EndZ=0
    g6: Circle [constr] CenterX=-44 CenterY=-38 CenterZ=0 NormalX=0 NormalY=0 NormalZ=1 Radius=3.5
  constraints (17):
    c: Coincident(g0,g1)
    c: Coincident(g1,g2)
    c: Coincident(g2,g3)
    c: Coincident(g3,g4)
    c: Coincident(g4,g5)
    c: Coincident(g5,g0)
    c: Equal(g0, g1-g5) x5
    c: PointOnObject(g0,g6)
    c: PointOnObject(g1,g6)
    c: PointOnObject(g2,g6)
    c: PointOnObject(g3,g6)
    c: PointOnObject(g4,g6)
    c: PointOnObject(g5,g6)
    c: Horizontal(g4)
    c: Radius(g6) = 3.5
    c: DistanceX(g-1,g6) = -44
    c: DistanceY(g-1,g6) = -38
FEATURE [PartDesign::Pad] Pad023
  Length = 10
  Length2 = 100
  Placement = pos=(0,0,-1.45) rot=(1,0,0;3.14159rad)
  Sketch = -> Sketch058
  Type = 0
FEATURE [Part::MultiFuse] Fusion055013
  Shapes = -> [Pad023,Cylinder059]
FEATURE [Part::Cylinder] Cylinder061  label="Cylinder065"
  Angle = 360
  Height = 8
  Placement = pos=(-44,38,5) rot=(0,0,1;0rad)
  Radius = 3
FEATURE [Sketcher::SketchObject] Sketch060
  Placement = pos=(0,0,-1.45) rot=(1,0,0;3.14159rad)
  sketch-geometry (7):
    g0: LineSegment StartX=-47.5 StartY=-38 StartZ=0 EndX=-45.75 EndY=-41.0311 EndZ=0
    g1: LineSegment StartX=-45.75 StartY=-41.0311 StartZ=0 EndX=-42.25 EndY=-41.0311 EndZ=0
    g2: LineSegment StartX=-42.25 StartY=-41.0311 StartZ=0 EndX=-40.5 EndY=-38 EndZ=0
    g3: LineSegment StartX=-40.5 StartY=-38 StartZ=0 EndX=-42.25 EndY=-34.9689 EndZ=0
    g4: LineSegment StartX=-42.25 StartY=-34.9689 StartZ=0 EndX=-45.75 EndY=-34.9689 EndZ=0
    g5: LineSegment StartX=-45.75 StartY=-34.9689 StartZ=0 EndX=-47.5 EndY=-38 EndZ=0
    g6: Circle [constr] CenterX=-44 CenterY=-38 CenterZ=0 NormalX=0 NormalY=0 NormalZ=1 Radius=3.5
  constraints (17):
    c: Coincident(g0,g1)
    c: Coincident(g1,g2)
    c: Coincident(g2,g3)
    c: Coincident(g3,g4)
    c: Coincident(g4,g5)
    c: Coincident(g5,g0)
    c: Equal(g0, g1-g5) x5
    c: PointOnObject(g0,g6)
    c: PointOnObject(g1,g6)
    c: PointOnObject(g2,g6)
    c: PointOnObject(g3,g6)
    c: PointOnObject(g4,g6)
    c: PointOnObject(g5,g6)
    c: Horizontal(g4)
    c: Radius(g6) = 3.5
    c: DistanceX(g-1,g6) = -44
    c: DistanceY(g-1,g6) = -38
FEATURE [PartDesign::Pad] Pad025
  Length = 10
  Length2 = 100
  Placement = pos=(0,0,-1.45) rot=(1,0,0;3.14159rad)
  Sketch = -> Sketch060
  Type = 0
FEATURE [Part::MultiFuse] Fusion055015
  Placement = pos=(0,-76,0) rot=(0,0,1;0rad)
  Shapes = -> [Pad025,Cylinder061]
FEATURE [Part::MultiFuse] Fusion055016
  Shapes = -> [Fusion055013,Fusion055015]
FEATURE [Part::Cut] Cut048015  label="Soportes_portapilas"
  Base = -> Fusion055010
  Tool = -> Fusion055016
FEATURE [Part::Box] Box  label="Cubo"
  Height = 46
  Length = 90
  Placement = pos=(-82,-36,14) rot=(0,0,1;0rad)
  Width = 72
FEATURE [Part::Cut] Cut
  Base = -> Cut048015
  Placement = pos=(0,1,0) rot=(0,0,1;0rad)
  Tool = -> Box
FEATURE [Part::Box] Box020  label="Cubo001"
  Height = 14
  Length = 3
  Placement = pos=(-57,-15,0) rot=(0,0,1;0rad)
  Width = 32
FEATURE [Part::MultiFuse] Fusion  label="PortabateriasCortado"
  Shapes = -> [Box020,Cut]
